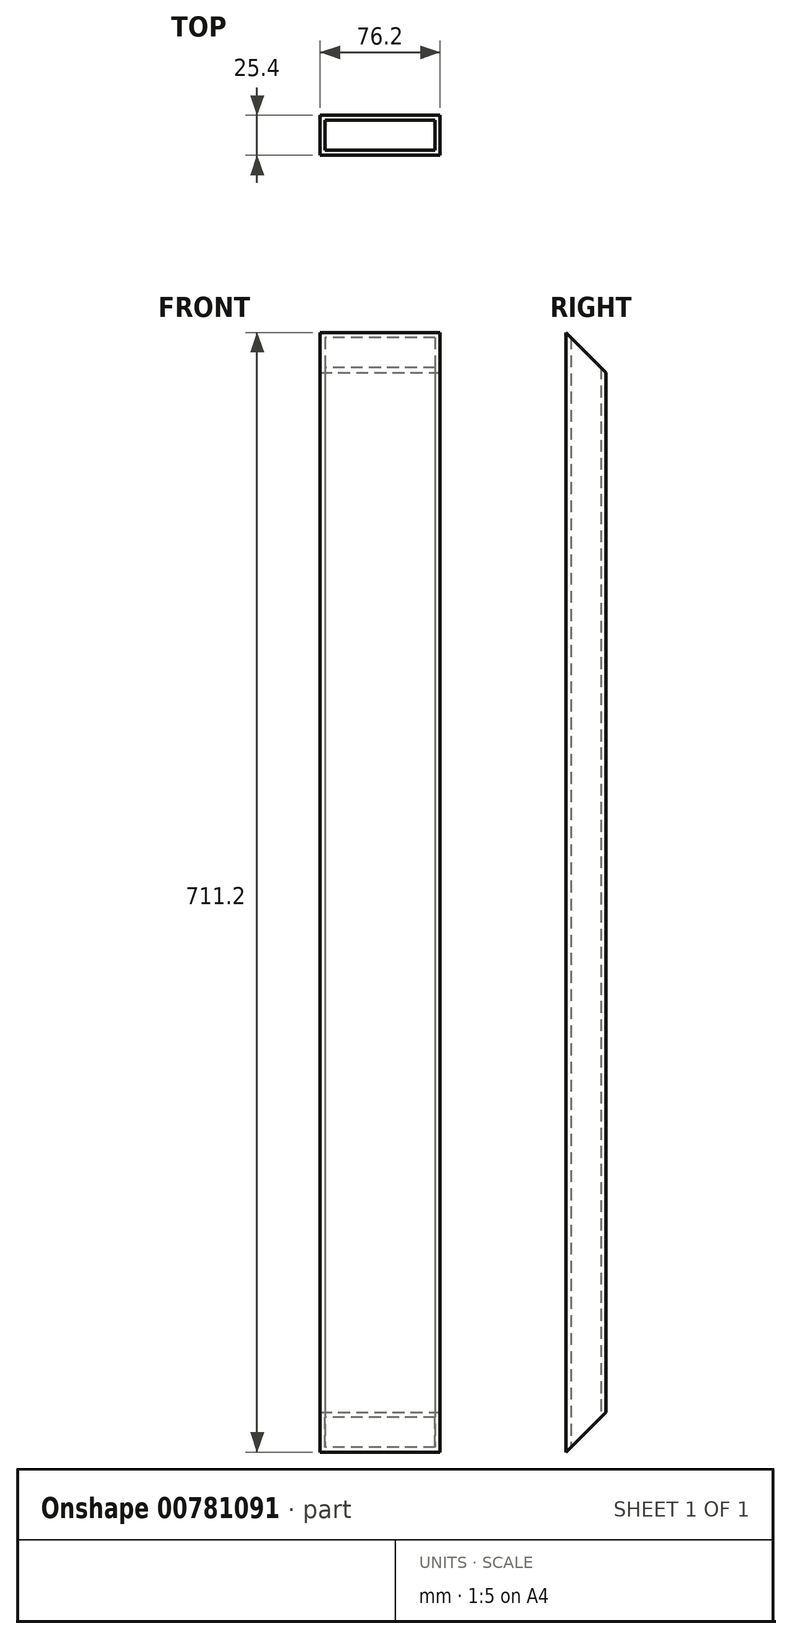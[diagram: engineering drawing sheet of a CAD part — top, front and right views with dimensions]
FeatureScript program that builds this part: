
annotation { "Feature Type Name" : "Feature", "Feature Type Description" : "" }
export const myFeature = defineFeature(function(context is Context, id is Id, definition is map)
    precondition{}
    {
        {
            var Q0;
            Q0=qCreatedBy(makeId("Top.planeOp"),FACE);
            var sketch = newSketch(context, id + "F0", { "sketchPlane" : qUnion([Q0])});
            skLineSegment(sketch, "E0.bottom", {"start": v(0, 0) * mm, "end": v(76.2, 0) * mm});
            skLineSegment(sketch, "E0.top", {"start": v(0, -25.4) * mm, "end": v(76.2, -25.4) * mm});
            skLineSegment(sketch, "E0.left", {"start": v(0, 0) * mm, "end": v(0, -25.4) * mm});
            skLineSegment(sketch, "E0.right", {"start": v(76.2, 0) * mm, "end": v(76.2, -25.4) * mm});
            skLineSegment(sketch, "E1.bottom", {"start": v(3.17, -3.18) * mm, "end": v(73.03, -3.18) * mm});
            skLineSegment(sketch, "E1.top", {"start": v(3.18, -22.23) * mm, "end": v(73.03, -22.23) * mm});
            skLineSegment(sketch, "E1.left", {"start": v(3.18, -3.18) * mm, "end": v(3.18, -22.23) * mm});
            skLineSegment(sketch, "E1.right", {"start": v(73.03, -3.18) * mm, "end": v(73.03, -22.23) * mm});
            skSolve(sketch);
        }
        {
            var Q0;
            Q0=makeQuery(id+"F0.imprint","IMPRINT",FACE,{"disambiguationData":[TD([[makeQuery(id+"F0.imprint","IMPRINT",EDGE,{"derivedFrom":sQuery(id+"F0.wireOp",EDGE,"E0.bottom")}),-1.0]])]});
            extrude(context, id + "F1", {"entities" : qUnion([Q0]), "depth" : 355.6 * mm, "offsetDistance" : 25.4 * mm, "hasSecondDirection" : true, "secondDirectionOppositeDirection" : true, "secondDirectionDepth" : 355.6 * mm});
        }
        {
            var Q0;
            Q0=makeQuery(id+"F1.opExtrude","SWEPT_FACE",FACE,{"disambiguationData":[OSD([sQuery(id+"F0.wireOp",EDGE,"E0.right")])]});
            var sketch = newSketch(context, id + "F2", { "sketchPlane" : qUnion([Q0])});
            skLineSegment(sketch, "E2", {"start": v(-25.4, 355.6) * mm, "end": v(0, 330.2) * mm});
            skLineSegment(sketch, "E3", {"start": v(0, 330.2) * mm, "end": v(0, 355.6) * mm});
            skLineSegment(sketch, "E4", {"start": v(0, 355.6) * mm, "end": v(-25.4, 355.6) * mm});
            skLineSegment(sketch, "E5.MirrorCS", {"start": v(-25.4, -355.6) * mm, "end": v(0, -330.2) * mm});
            skLineSegment(sketch, "E6.MirrorCS", {"start": v(0, -330.2) * mm, "end": v(0, -355.6) * mm});
            skLineSegment(sketch, "E7.MirrorCS", {"start": v(0, -355.6) * mm, "end": v(-25.4, -355.6) * mm});
            skSolve(sketch);
        }
        {
            var Q0;
            Q0=makeQuery(id+"F2.imprint","IMPRINT",FACE,{"disambiguationData":[TD([[makeQuery(id+"F2.imprint","IMPRINT",EDGE,{"derivedFrom":sQuery(id+"F2.wireOp",EDGE,"E2")}),1.0]])]});
            var Q1;
            Q1=makeQuery(id+"F2.imprint","IMPRINT",FACE,{"disambiguationData":[TD([[makeQuery(id+"F2.imprint","IMPRINT",EDGE,{"derivedFrom":sQuery(id+"F2.wireOp",EDGE,"E5.MirrorCS")}),-1.0]])]});
            extrude(context, id + "F3", {"entities" : qUnion([Q0, Q1]), "operationType" : NewBodyOperationType.REMOVE, "endBound" : BoundingType.THROUGH_ALL, "oppositeDirection" : true, "depth" : 25.4 * mm, "offsetDistance" : 25.4 * mm});
        }
    });
